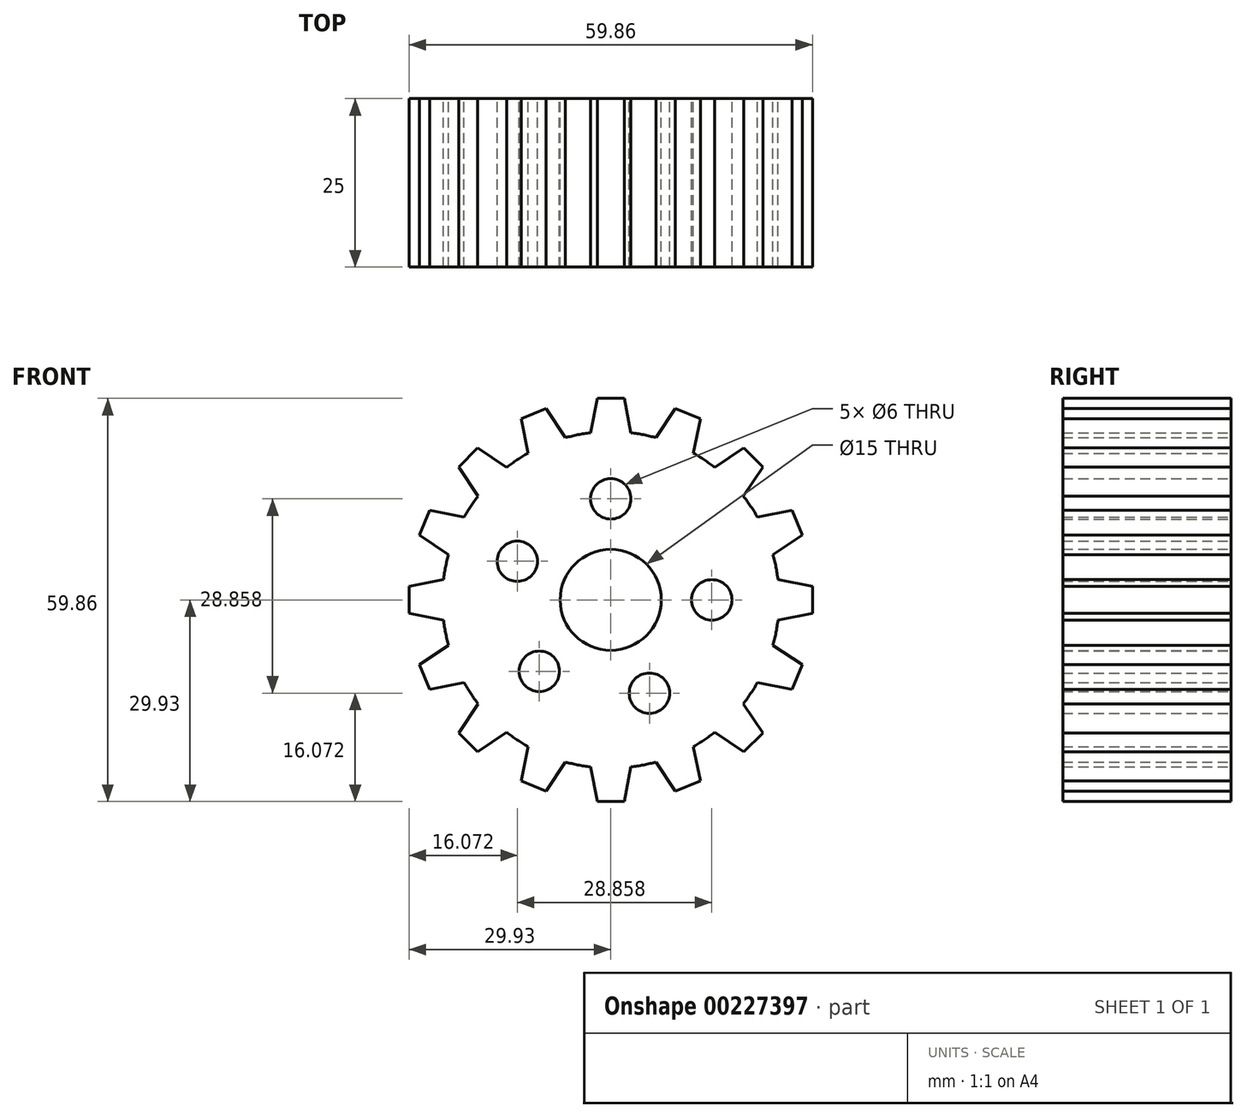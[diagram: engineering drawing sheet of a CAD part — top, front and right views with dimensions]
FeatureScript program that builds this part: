
annotation { "Feature Type Name" : "Feature", "Feature Type Description" : "" }
export const myFeature = defineFeature(function(context is Context, id is Id, definition is map)
    precondition{}
    {
        {
            var Q0;
            Q0=qCreatedBy(makeId("Front.planeOp"),FACE);
            var sketch = newSketch(context, id + "F0", { "sketchPlane" : qUnion([Q0])});
            skCircle(sketch, "E0", {"center": v(0, 0) * mm, "radius": 25 * mm});
            skLineSegment(sketch, "E1", {"start": v(2, 29.93) * mm, "end": v(-2, 29.93) * mm});
            skLineSegment(sketch, "E2", {"start": v(-2, 29.93) * mm, "end": v(-3, 24.82) * mm});
            skLineSegment(sketch, "E3", {"start": v(2, 29.93) * mm, "end": v(3, 24.82) * mm});
            skLineSegment(sketch, "E4", {"start": v(0, 0) * mm, "end": v(0, 41.14) * mm, "construction": true});
            skLineSegment(sketch, "E5.1.1", {"start": v(-13.3, 26.89) * mm, "end": v(-12.27, 21.78) * mm});
            skLineSegment(sketch, "E5.1.2", {"start": v(-9.6, 28.42) * mm, "end": v(-6.73, 24.08) * mm});
            skLineSegment(sketch, "E5.1.3", {"start": v(-9.6, 28.42) * mm, "end": v(-13.3, 26.89) * mm});
            skLineSegment(sketch, "E5.2.1", {"start": v(-22.58, 19.75) * mm, "end": v(-19.67, 15.43) * mm});
            skLineSegment(sketch, "E5.2.2", {"start": v(-19.75, 22.58) * mm, "end": v(-15.43, 19.67) * mm});
            skLineSegment(sketch, "E5.2.3", {"start": v(-19.75, 22.58) * mm, "end": v(-22.58, 19.75) * mm});
            skLineSegment(sketch, "E5.3.1", {"start": v(-28.42, 9.6) * mm, "end": v(-24.08, 6.73) * mm});
            skLineSegment(sketch, "E5.3.2", {"start": v(-26.89, 13.3) * mm, "end": v(-21.78, 12.27) * mm});
            skLineSegment(sketch, "E5.3.3", {"start": v(-26.89, 13.3) * mm, "end": v(-28.42, 9.6) * mm});
            skLineSegment(sketch, "E5.4.1", {"start": v(-29.93, -2) * mm, "end": v(-24.82, -3) * mm});
            skLineSegment(sketch, "E5.4.2", {"start": v(-29.93, 2) * mm, "end": v(-24.82, 3) * mm});
            skLineSegment(sketch, "E5.4.3", {"start": v(-29.93, 2) * mm, "end": v(-29.93, -2) * mm});
            skLineSegment(sketch, "E5.5.1", {"start": v(-26.89, -13.3) * mm, "end": v(-21.78, -12.27) * mm});
            skLineSegment(sketch, "E5.5.2", {"start": v(-28.42, -9.6) * mm, "end": v(-24.08, -6.73) * mm});
            skLineSegment(sketch, "E5.5.3", {"start": v(-28.42, -9.6) * mm, "end": v(-26.89, -13.3) * mm});
            skLineSegment(sketch, "E5.6.1", {"start": v(-19.75, -22.58) * mm, "end": v(-15.43, -19.67) * mm});
            skLineSegment(sketch, "E5.6.2", {"start": v(-22.58, -19.75) * mm, "end": v(-19.67, -15.43) * mm});
            skLineSegment(sketch, "E5.6.3", {"start": v(-22.58, -19.75) * mm, "end": v(-19.75, -22.58) * mm});
            skLineSegment(sketch, "E5.7.1", {"start": v(-9.6, -28.42) * mm, "end": v(-6.73, -24.08) * mm});
            skLineSegment(sketch, "E5.7.2", {"start": v(-13.3, -26.89) * mm, "end": v(-12.27, -21.78) * mm});
            skLineSegment(sketch, "E5.7.3", {"start": v(-13.3, -26.89) * mm, "end": v(-9.6, -28.42) * mm});
            skLineSegment(sketch, "E5.8.1", {"start": v(2, -29.93) * mm, "end": v(3, -24.82) * mm});
            skLineSegment(sketch, "E5.8.2", {"start": v(-2, -29.93) * mm, "end": v(-3, -24.82) * mm});
            skLineSegment(sketch, "E5.8.3", {"start": v(-2, -29.93) * mm, "end": v(2, -29.93) * mm});
            skLineSegment(sketch, "E5.9.1", {"start": v(13.3, -26.89) * mm, "end": v(12.27, -21.78) * mm});
            skLineSegment(sketch, "E5.9.2", {"start": v(9.6, -28.42) * mm, "end": v(6.73, -24.08) * mm});
            skLineSegment(sketch, "E5.9.3", {"start": v(9.6, -28.42) * mm, "end": v(13.3, -26.89) * mm});
            skLineSegment(sketch, "E5.10.1", {"start": v(22.58, -19.75) * mm, "end": v(19.67, -15.43) * mm});
            skLineSegment(sketch, "E5.10.2", {"start": v(19.75, -22.58) * mm, "end": v(15.43, -19.67) * mm});
            skLineSegment(sketch, "E5.10.3", {"start": v(19.75, -22.58) * mm, "end": v(22.58, -19.75) * mm});
            skLineSegment(sketch, "E5.11.1", {"start": v(28.42, -9.6) * mm, "end": v(24.08, -6.73) * mm});
            skLineSegment(sketch, "E5.11.2", {"start": v(26.89, -13.3) * mm, "end": v(21.78, -12.27) * mm});
            skLineSegment(sketch, "E5.11.3", {"start": v(26.89, -13.3) * mm, "end": v(28.42, -9.6) * mm});
            skLineSegment(sketch, "E5.12.1", {"start": v(29.93, 2) * mm, "end": v(24.82, 3) * mm});
            skLineSegment(sketch, "E5.12.2", {"start": v(29.93, -2) * mm, "end": v(24.82, -3) * mm});
            skLineSegment(sketch, "E5.12.3", {"start": v(29.93, -2) * mm, "end": v(29.93, 2) * mm});
            skLineSegment(sketch, "E5.13.1", {"start": v(26.89, 13.3) * mm, "end": v(21.78, 12.27) * mm});
            skLineSegment(sketch, "E5.13.2", {"start": v(28.42, 9.6) * mm, "end": v(24.08, 6.73) * mm});
            skLineSegment(sketch, "E5.13.3", {"start": v(28.42, 9.6) * mm, "end": v(26.89, 13.3) * mm});
            skLineSegment(sketch, "E5.14.1", {"start": v(19.75, 22.58) * mm, "end": v(15.43, 19.67) * mm});
            skLineSegment(sketch, "E5.14.2", {"start": v(22.58, 19.75) * mm, "end": v(19.67, 15.43) * mm});
            skLineSegment(sketch, "E5.14.3", {"start": v(22.58, 19.75) * mm, "end": v(19.75, 22.58) * mm});
            skLineSegment(sketch, "E5.15.1", {"start": v(9.6, 28.42) * mm, "end": v(6.73, 24.08) * mm});
            skLineSegment(sketch, "E5.15.2", {"start": v(13.3, 26.89) * mm, "end": v(12.27, 21.78) * mm});
            skLineSegment(sketch, "E5.15.3", {"start": v(13.3, 26.89) * mm, "end": v(9.6, 28.42) * mm});
            skCircle(sketch, "E6", {"center": v(0, 0) * mm, "radius": 7.5 * mm});
            skCircle(sketch, "E7", {"center": v(0, 0) * mm, "radius": 15 * mm, "construction": true});
            skPoint(sketch, "E8", {"position": v(0, 15) * mm});
            skCircle(sketch, "E9", {"center": v(0, 15) * mm, "radius": 3 * mm});
            skCircle(sketch, "E10.1.0", {"center": v(-13.86, 5.74) * mm, "radius": 3 * mm});
            skCircle(sketch, "E10.2.0", {"center": v(-10.6, -10.6) * mm, "radius": 3 * mm});
            skCircle(sketch, "E10.3.0", {"center": v(5.74, -13.86) * mm, "radius": 3 * mm});
            skCircle(sketch, "E10.4.0", {"center": v(15, 0) * mm, "radius": 3 * mm});
            skLineSegment(sketch, "E10.anchor1", {"start": v(0, 0) * mm, "end": v(0, 15) * mm, "construction": true});
            skLineSegment(sketch, "E10.anchor2", {"start": v(0, 0) * mm, "end": v(15, 0) * mm, "construction": true});
            skSolve(sketch);
        }
        {
            var Q0;
            Q0 = qSketchRegion(id + "F0", true);
            extrude(context, id + "F1", {"entities" : qUnion([Q0]), "depth" : 25 * mm});
        }
    });
